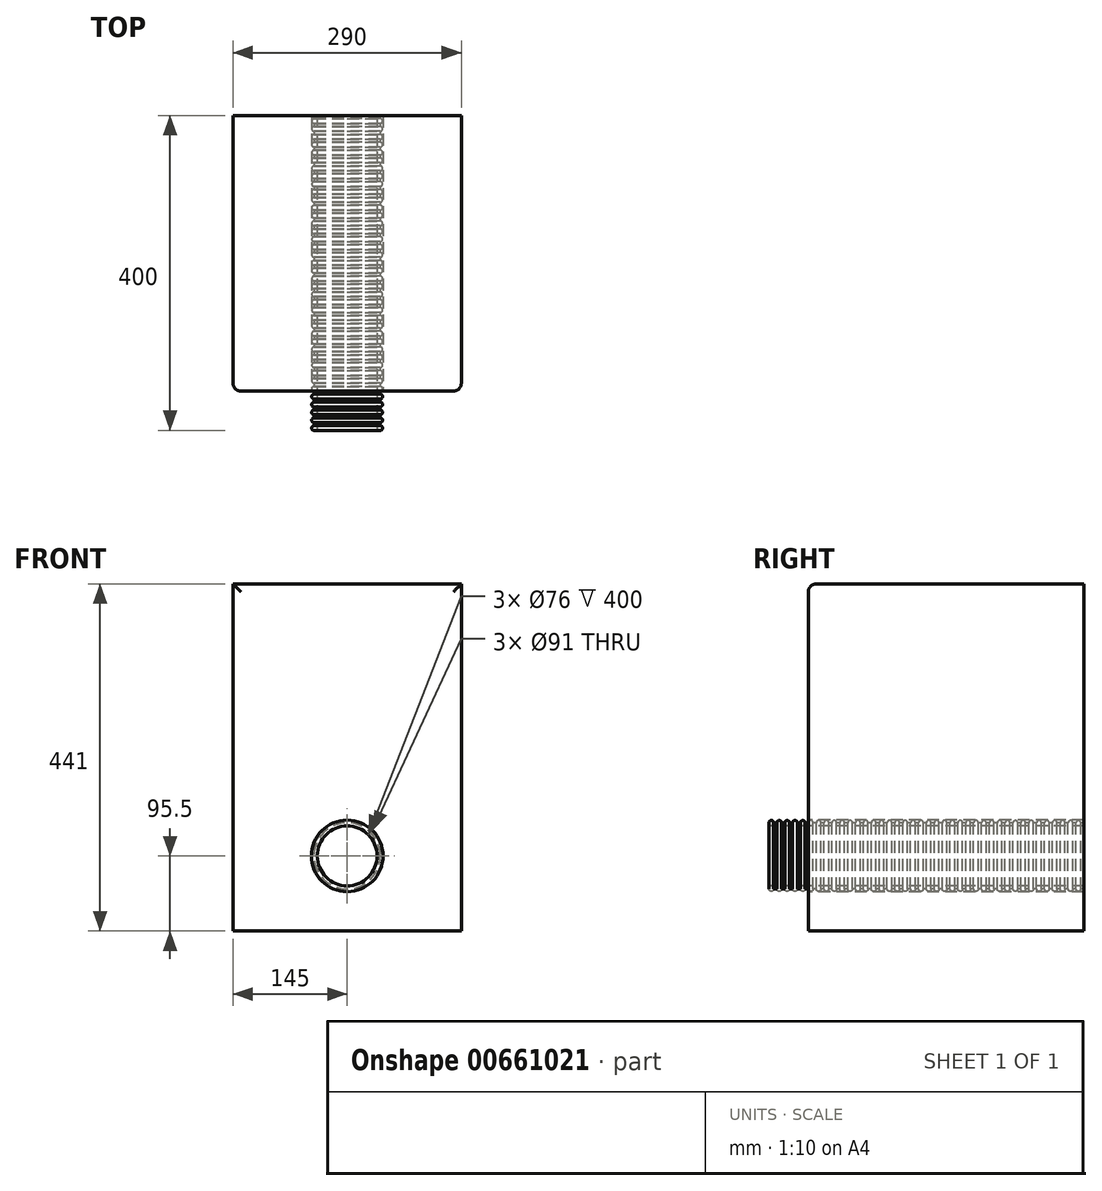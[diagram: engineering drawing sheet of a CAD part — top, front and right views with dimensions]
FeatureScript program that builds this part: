
annotation { "Feature Type Name" : "Feature", "Feature Type Description" : "" }
export const myFeature = defineFeature(function(context is Context, id is Id, definition is map)
    precondition{}
    {
        {
            var Q0;
            Q0=qCreatedBy(makeId("Right.planeOp"),FACE);
            var sketch = newSketch(context, id + "F0", { "sketchPlane" : qUnion([Q0])});
            skLineSegment(sketch, "E0", {"start": v(0, 0) * mm, "end": v(400, 0) * mm, "construction": true});
            skLineSegment(sketch, "E1", {"start": v(0, 38) * mm, "end": v(400, 38) * mm});
            skLineSegment(sketch, "E2", {"start": v(0, 38) * mm, "end": v(0, 42) * mm});
            skArc(sketch, "E3", {"start": v(6, 42) * mm, "mid": v(3, 45) * mm, "end": v(0, 42) * mm});
            skLineSegment(sketch, "E4", {"start": v(6, 42) * mm, "end": v(10, 42) * mm});
            skLineSegment(sketch, "E5.1.0.0", {"start": v(10, 38) * mm, "end": v(10, 42) * mm});
            skLineSegment(sketch, "E5.direction1", {"start": v(0, 38) * mm, "end": v(10, 38) * mm, "construction": true});
            skLineSegment(sketch, "E6.1.0.0", {"start": v(10, 38) * mm, "end": v(20, 38) * mm, "construction": true});
            skLineSegment(sketch, "E6.1.0.1", {"start": v(20, 38) * mm, "end": v(20, 42) * mm});
            skLineSegment(sketch, "E6.1.0.2", {"start": v(16, 42) * mm, "end": v(20, 42) * mm});
            skArc(sketch, "E6.1.0.3", {"start": v(16, 42) * mm, "mid": v(13, 45) * mm, "end": v(10, 42) * mm});
            skLineSegment(sketch, "E6.2.0.0", {"start": v(20, 38) * mm, "end": v(30, 38) * mm, "construction": true});
            skLineSegment(sketch, "E6.2.0.1", {"start": v(30, 38) * mm, "end": v(30, 42) * mm});
            skLineSegment(sketch, "E6.2.0.2", {"start": v(26, 42) * mm, "end": v(30, 42) * mm});
            skArc(sketch, "E6.2.0.3", {"start": v(26, 42) * mm, "mid": v(23, 45) * mm, "end": v(20, 42) * mm});
            skLineSegment(sketch, "E6.2.0.4", {"start": v(20, 38) * mm, "end": v(20, 42) * mm});
            skLineSegment(sketch, "E6.3.0.0", {"start": v(30, 38) * mm, "end": v(40, 38) * mm, "construction": true});
            skLineSegment(sketch, "E6.3.0.1", {"start": v(40, 38) * mm, "end": v(40, 42) * mm});
            skLineSegment(sketch, "E6.3.0.2", {"start": v(36, 42) * mm, "end": v(40, 42) * mm});
            skArc(sketch, "E6.3.0.3", {"start": v(36, 42) * mm, "mid": v(33, 45) * mm, "end": v(30, 42) * mm});
            skLineSegment(sketch, "E6.3.0.4", {"start": v(30, 38) * mm, "end": v(30, 42) * mm});
            skLineSegment(sketch, "E6.4.0.0", {"start": v(40, 38) * mm, "end": v(50, 38) * mm, "construction": true});
            skLineSegment(sketch, "E6.4.0.1", {"start": v(50, 38) * mm, "end": v(50, 42) * mm});
            skLineSegment(sketch, "E6.4.0.2", {"start": v(46, 42) * mm, "end": v(50, 42) * mm});
            skArc(sketch, "E6.4.0.3", {"start": v(46, 42) * mm, "mid": v(43, 45) * mm, "end": v(40, 42) * mm});
            skLineSegment(sketch, "E6.4.0.4", {"start": v(40, 38) * mm, "end": v(40, 42) * mm});
            skLineSegment(sketch, "E6.5.0.0", {"start": v(50, 38) * mm, "end": v(60, 38) * mm, "construction": true});
            skLineSegment(sketch, "E6.5.0.1", {"start": v(60, 38) * mm, "end": v(60, 42) * mm});
            skLineSegment(sketch, "E6.5.0.2", {"start": v(56, 42) * mm, "end": v(60, 42) * mm});
            skArc(sketch, "E6.5.0.3", {"start": v(56, 42) * mm, "mid": v(53, 45) * mm, "end": v(50, 42) * mm});
            skLineSegment(sketch, "E6.5.0.4", {"start": v(50, 38) * mm, "end": v(50, 42) * mm});
            skLineSegment(sketch, "E6.6.0.0", {"start": v(60, 38) * mm, "end": v(70, 38) * mm, "construction": true});
            skLineSegment(sketch, "E6.6.0.1", {"start": v(70, 38) * mm, "end": v(70, 42) * mm});
            skLineSegment(sketch, "E6.6.0.2", {"start": v(66, 42) * mm, "end": v(70, 42) * mm});
            skArc(sketch, "E6.6.0.3", {"start": v(66, 42) * mm, "mid": v(63, 45) * mm, "end": v(60, 42) * mm});
            skLineSegment(sketch, "E6.6.0.4", {"start": v(60, 38) * mm, "end": v(60, 42) * mm});
            skLineSegment(sketch, "E6.7.0.0", {"start": v(70, 38) * mm, "end": v(80, 38) * mm, "construction": true});
            skLineSegment(sketch, "E6.7.0.1", {"start": v(80, 38) * mm, "end": v(80, 42) * mm});
            skLineSegment(sketch, "E6.7.0.2", {"start": v(76, 42) * mm, "end": v(80, 42) * mm});
            skArc(sketch, "E6.7.0.3", {"start": v(76, 42) * mm, "mid": v(73, 45) * mm, "end": v(70, 42) * mm});
            skLineSegment(sketch, "E6.7.0.4", {"start": v(70, 38) * mm, "end": v(70, 42) * mm});
            skLineSegment(sketch, "E6.8.0.0", {"start": v(80, 38) * mm, "end": v(90, 38) * mm, "construction": true});
            skLineSegment(sketch, "E6.8.0.1", {"start": v(90, 38) * mm, "end": v(90, 42) * mm});
            skLineSegment(sketch, "E6.8.0.2", {"start": v(86, 42) * mm, "end": v(90, 42) * mm});
            skArc(sketch, "E6.8.0.3", {"start": v(86, 42) * mm, "mid": v(83, 45) * mm, "end": v(80, 42) * mm});
            skLineSegment(sketch, "E6.8.0.4", {"start": v(80, 38) * mm, "end": v(80, 42) * mm});
            skLineSegment(sketch, "E6.9.0.0", {"start": v(90, 38) * mm, "end": v(100, 38) * mm, "construction": true});
            skLineSegment(sketch, "E6.9.0.1", {"start": v(100, 38) * mm, "end": v(100, 42) * mm});
            skLineSegment(sketch, "E6.9.0.2", {"start": v(96, 42) * mm, "end": v(100, 42) * mm});
            skArc(sketch, "E6.9.0.3", {"start": v(96, 42) * mm, "mid": v(93, 45) * mm, "end": v(90, 42) * mm});
            skLineSegment(sketch, "E6.9.0.4", {"start": v(90, 38) * mm, "end": v(90, 42) * mm});
            skLineSegment(sketch, "E6.10.0.0", {"start": v(100, 38) * mm, "end": v(110, 38) * mm, "construction": true});
            skLineSegment(sketch, "E6.10.0.1", {"start": v(110, 38) * mm, "end": v(110, 42) * mm});
            skLineSegment(sketch, "E6.10.0.2", {"start": v(106, 42) * mm, "end": v(110, 42) * mm});
            skArc(sketch, "E6.10.0.3", {"start": v(106, 42) * mm, "mid": v(103, 45) * mm, "end": v(100, 42) * mm});
            skLineSegment(sketch, "E6.10.0.4", {"start": v(100, 38) * mm, "end": v(100, 42) * mm});
            skLineSegment(sketch, "E6.11.0.0", {"start": v(110, 38) * mm, "end": v(120, 38) * mm, "construction": true});
            skLineSegment(sketch, "E6.11.0.1", {"start": v(120, 38) * mm, "end": v(120, 42) * mm});
            skLineSegment(sketch, "E6.11.0.2", {"start": v(116, 42) * mm, "end": v(120, 42) * mm});
            skArc(sketch, "E6.11.0.3", {"start": v(116, 42) * mm, "mid": v(113, 45) * mm, "end": v(110, 42) * mm});
            skLineSegment(sketch, "E6.11.0.4", {"start": v(110, 38) * mm, "end": v(110, 42) * mm});
            skLineSegment(sketch, "E6.12.0.0", {"start": v(120, 38) * mm, "end": v(130, 38) * mm, "construction": true});
            skLineSegment(sketch, "E6.12.0.1", {"start": v(130, 38) * mm, "end": v(130, 42) * mm});
            skLineSegment(sketch, "E6.12.0.2", {"start": v(126, 42) * mm, "end": v(130, 42) * mm});
            skArc(sketch, "E6.12.0.3", {"start": v(126, 42) * mm, "mid": v(123, 45) * mm, "end": v(120, 42) * mm});
            skLineSegment(sketch, "E6.12.0.4", {"start": v(120, 38) * mm, "end": v(120, 42) * mm});
            skLineSegment(sketch, "E6.13.0.0", {"start": v(130, 38) * mm, "end": v(140, 38) * mm, "construction": true});
            skLineSegment(sketch, "E6.13.0.1", {"start": v(140, 38) * mm, "end": v(140, 42) * mm});
            skLineSegment(sketch, "E6.13.0.2", {"start": v(136, 42) * mm, "end": v(140, 42) * mm});
            skArc(sketch, "E6.13.0.3", {"start": v(136, 42) * mm, "mid": v(133, 45) * mm, "end": v(130, 42) * mm});
            skLineSegment(sketch, "E6.13.0.4", {"start": v(130, 38) * mm, "end": v(130, 42) * mm});
            skLineSegment(sketch, "E6.14.0.0", {"start": v(140, 38) * mm, "end": v(150, 38) * mm, "construction": true});
            skLineSegment(sketch, "E6.14.0.1", {"start": v(150, 38) * mm, "end": v(150, 42) * mm});
            skLineSegment(sketch, "E6.14.0.2", {"start": v(146, 42) * mm, "end": v(150, 42) * mm});
            skArc(sketch, "E6.14.0.3", {"start": v(146, 42) * mm, "mid": v(143, 45) * mm, "end": v(140, 42) * mm});
            skLineSegment(sketch, "E6.14.0.4", {"start": v(140, 38) * mm, "end": v(140, 42) * mm});
            skLineSegment(sketch, "E6.15.0.0", {"start": v(150, 38) * mm, "end": v(160, 38) * mm, "construction": true});
            skLineSegment(sketch, "E6.15.0.1", {"start": v(160, 38) * mm, "end": v(160, 42) * mm});
            skLineSegment(sketch, "E6.15.0.2", {"start": v(156, 42) * mm, "end": v(160, 42) * mm});
            skArc(sketch, "E6.15.0.3", {"start": v(156, 42) * mm, "mid": v(153, 45) * mm, "end": v(150, 42) * mm});
            skLineSegment(sketch, "E6.15.0.4", {"start": v(150, 38) * mm, "end": v(150, 42) * mm});
            skLineSegment(sketch, "E6.16.0.0", {"start": v(160, 38) * mm, "end": v(170, 38) * mm, "construction": true});
            skLineSegment(sketch, "E6.16.0.1", {"start": v(170, 38) * mm, "end": v(170, 42) * mm});
            skLineSegment(sketch, "E6.16.0.2", {"start": v(166, 42) * mm, "end": v(170, 42) * mm});
            skArc(sketch, "E6.16.0.3", {"start": v(166, 42) * mm, "mid": v(163, 45) * mm, "end": v(160, 42) * mm});
            skLineSegment(sketch, "E6.16.0.4", {"start": v(160, 38) * mm, "end": v(160, 42) * mm});
            skLineSegment(sketch, "E6.17.0.0", {"start": v(170, 38) * mm, "end": v(180, 38) * mm, "construction": true});
            skLineSegment(sketch, "E6.17.0.1", {"start": v(180, 38) * mm, "end": v(180, 42) * mm});
            skLineSegment(sketch, "E6.17.0.2", {"start": v(176, 42) * mm, "end": v(180, 42) * mm});
            skArc(sketch, "E6.17.0.3", {"start": v(176, 42) * mm, "mid": v(173, 45) * mm, "end": v(170, 42) * mm});
            skLineSegment(sketch, "E6.17.0.4", {"start": v(170, 38) * mm, "end": v(170, 42) * mm});
            skLineSegment(sketch, "E6.18.0.0", {"start": v(180, 38) * mm, "end": v(190, 38) * mm, "construction": true});
            skLineSegment(sketch, "E6.18.0.1", {"start": v(190, 38) * mm, "end": v(190, 42) * mm});
            skLineSegment(sketch, "E6.18.0.2", {"start": v(186, 42) * mm, "end": v(190, 42) * mm});
            skArc(sketch, "E6.18.0.3", {"start": v(186, 42) * mm, "mid": v(183, 45) * mm, "end": v(180, 42) * mm});
            skLineSegment(sketch, "E6.18.0.4", {"start": v(180, 38) * mm, "end": v(180, 42) * mm});
            skLineSegment(sketch, "E6.19.0.0", {"start": v(190, 38) * mm, "end": v(200, 38) * mm, "construction": true});
            skLineSegment(sketch, "E6.19.0.1", {"start": v(200, 38) * mm, "end": v(200, 42) * mm});
            skLineSegment(sketch, "E6.19.0.2", {"start": v(196, 42) * mm, "end": v(200, 42) * mm});
            skArc(sketch, "E6.19.0.3", {"start": v(196, 42) * mm, "mid": v(193, 45) * mm, "end": v(190, 42) * mm});
            skLineSegment(sketch, "E6.19.0.4", {"start": v(190, 38) * mm, "end": v(190, 42) * mm});
            skLineSegment(sketch, "E6.20.0.0", {"start": v(200, 38) * mm, "end": v(210, 38) * mm, "construction": true});
            skLineSegment(sketch, "E6.20.0.1", {"start": v(210, 38) * mm, "end": v(210, 42) * mm});
            skLineSegment(sketch, "E6.20.0.2", {"start": v(206, 42) * mm, "end": v(210, 42) * mm});
            skArc(sketch, "E6.20.0.3", {"start": v(206, 42) * mm, "mid": v(203, 45) * mm, "end": v(200, 42) * mm});
            skLineSegment(sketch, "E6.20.0.4", {"start": v(200, 38) * mm, "end": v(200, 42) * mm});
            skLineSegment(sketch, "E6.21.0.0", {"start": v(210, 38) * mm, "end": v(220, 38) * mm, "construction": true});
            skLineSegment(sketch, "E6.21.0.1", {"start": v(220, 38) * mm, "end": v(220, 42) * mm});
            skLineSegment(sketch, "E6.21.0.2", {"start": v(216, 42) * mm, "end": v(220, 42) * mm});
            skArc(sketch, "E6.21.0.3", {"start": v(216, 42) * mm, "mid": v(213, 45) * mm, "end": v(210, 42) * mm});
            skLineSegment(sketch, "E6.21.0.4", {"start": v(210, 38) * mm, "end": v(210, 42) * mm});
            skLineSegment(sketch, "E6.22.0.0", {"start": v(220, 38) * mm, "end": v(230, 38) * mm, "construction": true});
            skLineSegment(sketch, "E6.22.0.1", {"start": v(230, 38) * mm, "end": v(230, 42) * mm});
            skLineSegment(sketch, "E6.22.0.2", {"start": v(226, 42) * mm, "end": v(230, 42) * mm});
            skArc(sketch, "E6.22.0.3", {"start": v(226, 42) * mm, "mid": v(223, 45) * mm, "end": v(220, 42) * mm});
            skLineSegment(sketch, "E6.22.0.4", {"start": v(220, 38) * mm, "end": v(220, 42) * mm});
            skLineSegment(sketch, "E6.23.0.0", {"start": v(230, 38) * mm, "end": v(240, 38) * mm, "construction": true});
            skLineSegment(sketch, "E6.23.0.1", {"start": v(240, 38) * mm, "end": v(240, 42) * mm});
            skLineSegment(sketch, "E6.23.0.2", {"start": v(236, 42) * mm, "end": v(240, 42) * mm});
            skArc(sketch, "E6.23.0.3", {"start": v(236, 42) * mm, "mid": v(233, 45) * mm, "end": v(230, 42) * mm});
            skLineSegment(sketch, "E6.23.0.4", {"start": v(230, 38) * mm, "end": v(230, 42) * mm});
            skLineSegment(sketch, "E6.24.0.0", {"start": v(240, 38) * mm, "end": v(250, 38) * mm, "construction": true});
            skLineSegment(sketch, "E6.24.0.1", {"start": v(250, 38) * mm, "end": v(250, 42) * mm});
            skLineSegment(sketch, "E6.24.0.2", {"start": v(246, 42) * mm, "end": v(250, 42) * mm});
            skArc(sketch, "E6.24.0.3", {"start": v(246, 42) * mm, "mid": v(243, 45) * mm, "end": v(240, 42) * mm});
            skLineSegment(sketch, "E6.24.0.4", {"start": v(240, 38) * mm, "end": v(240, 42) * mm});
            skLineSegment(sketch, "E6.25.0.0", {"start": v(250, 38) * mm, "end": v(260, 38) * mm, "construction": true});
            skLineSegment(sketch, "E6.25.0.1", {"start": v(260, 38) * mm, "end": v(260, 42) * mm});
            skLineSegment(sketch, "E6.25.0.2", {"start": v(256, 42) * mm, "end": v(260, 42) * mm});
            skArc(sketch, "E6.25.0.3", {"start": v(256, 42) * mm, "mid": v(253, 45) * mm, "end": v(250, 42) * mm});
            skLineSegment(sketch, "E6.25.0.4", {"start": v(250, 38) * mm, "end": v(250, 42) * mm});
            skLineSegment(sketch, "E6.26.0.0", {"start": v(260, 38) * mm, "end": v(270, 38) * mm, "construction": true});
            skLineSegment(sketch, "E6.26.0.1", {"start": v(270, 38) * mm, "end": v(270, 42) * mm});
            skLineSegment(sketch, "E6.26.0.2", {"start": v(266, 42) * mm, "end": v(270, 42) * mm});
            skArc(sketch, "E6.26.0.3", {"start": v(266, 42) * mm, "mid": v(263, 45) * mm, "end": v(260, 42) * mm});
            skLineSegment(sketch, "E6.26.0.4", {"start": v(260, 38) * mm, "end": v(260, 42) * mm});
            skLineSegment(sketch, "E6.27.0.0", {"start": v(270, 38) * mm, "end": v(280, 38) * mm, "construction": true});
            skLineSegment(sketch, "E6.27.0.1", {"start": v(280, 38) * mm, "end": v(280, 42) * mm});
            skLineSegment(sketch, "E6.27.0.2", {"start": v(276, 42) * mm, "end": v(280, 42) * mm});
            skArc(sketch, "E6.27.0.3", {"start": v(276, 42) * mm, "mid": v(273, 45) * mm, "end": v(270, 42) * mm});
            skLineSegment(sketch, "E6.27.0.4", {"start": v(270, 38) * mm, "end": v(270, 42) * mm});
            skLineSegment(sketch, "E6.28.0.0", {"start": v(280, 38) * mm, "end": v(290, 38) * mm, "construction": true});
            skLineSegment(sketch, "E6.28.0.1", {"start": v(290, 38) * mm, "end": v(290, 42) * mm});
            skLineSegment(sketch, "E6.28.0.2", {"start": v(286, 42) * mm, "end": v(290, 42) * mm});
            skArc(sketch, "E6.28.0.3", {"start": v(286, 42) * mm, "mid": v(283, 45) * mm, "end": v(280, 42) * mm});
            skLineSegment(sketch, "E6.28.0.4", {"start": v(280, 38) * mm, "end": v(280, 42) * mm});
            skLineSegment(sketch, "E6.29.0.0", {"start": v(290, 38) * mm, "end": v(300, 38) * mm, "construction": true});
            skLineSegment(sketch, "E6.29.0.1", {"start": v(300, 38) * mm, "end": v(300, 42) * mm});
            skLineSegment(sketch, "E6.29.0.2", {"start": v(296, 42) * mm, "end": v(300, 42) * mm});
            skArc(sketch, "E6.29.0.3", {"start": v(296, 42) * mm, "mid": v(293, 45) * mm, "end": v(290, 42) * mm});
            skLineSegment(sketch, "E6.29.0.4", {"start": v(290, 38) * mm, "end": v(290, 42) * mm});
            skLineSegment(sketch, "E6.30.0.0", {"start": v(300, 38) * mm, "end": v(310, 38) * mm, "construction": true});
            skLineSegment(sketch, "E6.30.0.1", {"start": v(310, 38) * mm, "end": v(310, 42) * mm});
            skLineSegment(sketch, "E6.30.0.2", {"start": v(306, 42) * mm, "end": v(310, 42) * mm});
            skArc(sketch, "E6.30.0.3", {"start": v(306, 42) * mm, "mid": v(303, 45) * mm, "end": v(300, 42) * mm});
            skLineSegment(sketch, "E6.30.0.4", {"start": v(300, 38) * mm, "end": v(300, 42) * mm});
            skLineSegment(sketch, "E6.31.0.0", {"start": v(310, 38) * mm, "end": v(320, 38) * mm, "construction": true});
            skLineSegment(sketch, "E6.31.0.1", {"start": v(320, 38) * mm, "end": v(320, 42) * mm});
            skLineSegment(sketch, "E6.31.0.2", {"start": v(316, 42) * mm, "end": v(320, 42) * mm});
            skArc(sketch, "E6.31.0.3", {"start": v(316, 42) * mm, "mid": v(313, 45) * mm, "end": v(310, 42) * mm});
            skLineSegment(sketch, "E6.31.0.4", {"start": v(310, 38) * mm, "end": v(310, 42) * mm});
            skLineSegment(sketch, "E6.32.0.0", {"start": v(320, 38) * mm, "end": v(330, 38) * mm, "construction": true});
            skLineSegment(sketch, "E6.32.0.1", {"start": v(330, 38) * mm, "end": v(330, 42) * mm});
            skLineSegment(sketch, "E6.32.0.2", {"start": v(326, 42) * mm, "end": v(330, 42) * mm});
            skArc(sketch, "E6.32.0.3", {"start": v(326, 42) * mm, "mid": v(323, 45) * mm, "end": v(320, 42) * mm});
            skLineSegment(sketch, "E6.32.0.4", {"start": v(320, 38) * mm, "end": v(320, 42) * mm});
            skLineSegment(sketch, "E6.33.0.0", {"start": v(330, 38) * mm, "end": v(340, 38) * mm, "construction": true});
            skLineSegment(sketch, "E6.33.0.1", {"start": v(340, 38) * mm, "end": v(340, 42) * mm});
            skLineSegment(sketch, "E6.33.0.2", {"start": v(336, 42) * mm, "end": v(340, 42) * mm});
            skArc(sketch, "E6.33.0.3", {"start": v(336, 42) * mm, "mid": v(333, 45) * mm, "end": v(330, 42) * mm});
            skLineSegment(sketch, "E6.33.0.4", {"start": v(330, 38) * mm, "end": v(330, 42) * mm});
            skLineSegment(sketch, "E6.34.0.0", {"start": v(340, 38) * mm, "end": v(350, 38) * mm, "construction": true});
            skLineSegment(sketch, "E6.34.0.1", {"start": v(350, 38) * mm, "end": v(350, 42) * mm});
            skLineSegment(sketch, "E6.34.0.2", {"start": v(346, 42) * mm, "end": v(350, 42) * mm});
            skArc(sketch, "E6.34.0.3", {"start": v(346, 42) * mm, "mid": v(343, 45) * mm, "end": v(340, 42) * mm});
            skLineSegment(sketch, "E6.34.0.4", {"start": v(340, 38) * mm, "end": v(340, 42) * mm});
            skLineSegment(sketch, "E6.35.0.0", {"start": v(350, 38) * mm, "end": v(360, 38) * mm, "construction": true});
            skLineSegment(sketch, "E6.35.0.1", {"start": v(360, 38) * mm, "end": v(360, 42) * mm});
            skLineSegment(sketch, "E6.35.0.2", {"start": v(356, 42) * mm, "end": v(360, 42) * mm});
            skArc(sketch, "E6.35.0.3", {"start": v(356, 42) * mm, "mid": v(353, 45) * mm, "end": v(350, 42) * mm});
            skLineSegment(sketch, "E6.35.0.4", {"start": v(350, 38) * mm, "end": v(350, 42) * mm});
            skLineSegment(sketch, "E6.36.0.0", {"start": v(360, 38) * mm, "end": v(370, 38) * mm, "construction": true});
            skLineSegment(sketch, "E6.36.0.1", {"start": v(370, 38) * mm, "end": v(370, 42) * mm});
            skLineSegment(sketch, "E6.36.0.2", {"start": v(366, 42) * mm, "end": v(370, 42) * mm});
            skArc(sketch, "E6.36.0.3", {"start": v(366, 42) * mm, "mid": v(363, 45) * mm, "end": v(360, 42) * mm});
            skLineSegment(sketch, "E6.36.0.4", {"start": v(360, 38) * mm, "end": v(360, 42) * mm});
            skLineSegment(sketch, "E6.37.0.0", {"start": v(370, 38) * mm, "end": v(380, 38) * mm, "construction": true});
            skLineSegment(sketch, "E6.37.0.1", {"start": v(380, 38) * mm, "end": v(380, 42) * mm});
            skLineSegment(sketch, "E6.37.0.2", {"start": v(376, 42) * mm, "end": v(380, 42) * mm});
            skArc(sketch, "E6.37.0.3", {"start": v(376, 42) * mm, "mid": v(373, 45) * mm, "end": v(370, 42) * mm});
            skLineSegment(sketch, "E6.37.0.4", {"start": v(370, 38) * mm, "end": v(370, 42) * mm});
            skLineSegment(sketch, "E6.38.0.0", {"start": v(380, 38) * mm, "end": v(390, 38) * mm, "construction": true});
            skLineSegment(sketch, "E6.38.0.1", {"start": v(390, 38) * mm, "end": v(390, 42) * mm});
            skLineSegment(sketch, "E6.38.0.2", {"start": v(386, 42) * mm, "end": v(390, 42) * mm});
            skArc(sketch, "E6.38.0.3", {"start": v(386, 42) * mm, "mid": v(383, 45) * mm, "end": v(380, 42) * mm});
            skLineSegment(sketch, "E6.38.0.4", {"start": v(380, 38) * mm, "end": v(380, 42) * mm});
            skLineSegment(sketch, "E6.39.0.0", {"start": v(390, 38) * mm, "end": v(400, 38) * mm, "construction": true});
            skLineSegment(sketch, "E6.39.0.1", {"start": v(400, 38) * mm, "end": v(400, 42) * mm});
            skLineSegment(sketch, "E6.39.0.2", {"start": v(396, 42) * mm, "end": v(400, 42) * mm});
            skArc(sketch, "E6.39.0.3", {"start": v(396, 42) * mm, "mid": v(393, 45) * mm, "end": v(390, 42) * mm});
            skLineSegment(sketch, "E6.39.0.4", {"start": v(390, 38) * mm, "end": v(390, 42) * mm});
            skSolve(sketch);
        }
        {
            var Q0;
            {var subQ0=sQuery(id+"F0.wireOp",EDGE,"E6.39.0.1");Q0=makeQuery(id+"F0.imprint","IMPRINT",FACE,{"disambiguationData":[TD([[makeQuery(id+"F0.imprint","IMPRINT",EDGE,{"derivedFrom":subQ0}),1.0]])]});}
            var Q1;
            Q1=makeQuery(id+"F0.imprint","IMPRINT",FACE,{"disambiguationData":[TD([[makeQuery(id+"F0.imprint","IMPRINT",EDGE,{"derivedFrom":sQuery(id+"F0.wireOp",EDGE,"E6.30.0.2")}),-1.0]])]});
            var Q2;
            Q2=makeQuery(id+"F0.imprint","IMPRINT",FACE,{"disambiguationData":[TD([[makeQuery(id+"F0.imprint","IMPRINT",EDGE,{"derivedFrom":sQuery(id+"F0.wireOp",EDGE,"E6.23.0.2")}),-1.0]])]});
            var Q3;
            Q3=makeQuery(id+"F0.imprint","IMPRINT",FACE,{"disambiguationData":[TD([[makeQuery(id+"F0.imprint","IMPRINT",EDGE,{"derivedFrom":sQuery(id+"F0.wireOp",EDGE,"E6.24.0.2")}),-1.0]])]});
            var Q4;
            Q4=makeQuery(id+"F0.imprint","IMPRINT",FACE,{"disambiguationData":[TD([[makeQuery(id+"F0.imprint","IMPRINT",EDGE,{"derivedFrom":sQuery(id+"F0.wireOp",EDGE,"E6.4.0.2")}),-1.0]])]});
            var Q5;
            Q5=makeQuery(id+"F0.imprint","IMPRINT",FACE,{"disambiguationData":[TD([[makeQuery(id+"F0.imprint","IMPRINT",EDGE,{"derivedFrom":sQuery(id+"F0.wireOp",EDGE,"E6.9.0.2")}),-1.0]])]});
            var Q6;
            Q6=makeQuery(id+"F0.imprint","IMPRINT",FACE,{"disambiguationData":[TD([[makeQuery(id+"F0.imprint","IMPRINT",EDGE,{"derivedFrom":sQuery(id+"F0.wireOp",EDGE,"E6.10.0.2")}),-1.0]])]});
            var Q7;
            Q7=makeQuery(id+"F0.imprint","IMPRINT",FACE,{"disambiguationData":[TD([[makeQuery(id+"F0.imprint","IMPRINT",EDGE,{"derivedFrom":sQuery(id+"F0.wireOp",EDGE,"E6.5.0.2")}),-1.0]])]});
            var Q8;
            Q8=makeQuery(id+"F0.imprint","IMPRINT",FACE,{"disambiguationData":[TD([[makeQuery(id+"F0.imprint","IMPRINT",EDGE,{"derivedFrom":sQuery(id+"F0.wireOp",EDGE,"E6.7.0.2")}),-1.0]])]});
            var Q9;
            Q9=makeQuery(id+"F0.imprint","IMPRINT",FACE,{"disambiguationData":[TD([[makeQuery(id+"F0.imprint","IMPRINT",EDGE,{"derivedFrom":sQuery(id+"F0.wireOp",EDGE,"E6.8.0.2")}),-1.0]])]});
            var Q10;
            Q10=makeQuery(id+"F0.imprint","IMPRINT",FACE,{"disambiguationData":[TD([[makeQuery(id+"F0.imprint","IMPRINT",EDGE,{"derivedFrom":sQuery(id+"F0.wireOp",EDGE,"E6.12.0.2")}),-1.0]])]});
            var Q11;
            Q11=makeQuery(id+"F0.imprint","IMPRINT",FACE,{"disambiguationData":[TD([[makeQuery(id+"F0.imprint","IMPRINT",EDGE,{"derivedFrom":sQuery(id+"F0.wireOp",EDGE,"E6.14.0.2")}),-1.0]])]});
            var Q12;
            Q12=makeQuery(id+"F0.imprint","IMPRINT",FACE,{"disambiguationData":[TD([[makeQuery(id+"F0.imprint","IMPRINT",EDGE,{"derivedFrom":sQuery(id+"F0.wireOp",EDGE,"E6.21.0.2")}),-1.0]])]});
            var Q13;
            Q13=makeQuery(id+"F0.imprint","IMPRINT",FACE,{"disambiguationData":[TD([[makeQuery(id+"F0.imprint","IMPRINT",EDGE,{"derivedFrom":sQuery(id+"F0.wireOp",EDGE,"E6.37.0.2")}),-1.0]])]});
            var Q14;
            Q14=makeQuery(id+"F0.imprint","IMPRINT",FACE,{"disambiguationData":[TD([[makeQuery(id+"F0.imprint","IMPRINT",EDGE,{"derivedFrom":sQuery(id+"F0.wireOp",EDGE,"E6.36.0.2")}),-1.0]])]});
            var Q15;
            Q15=makeQuery(id+"F0.imprint","IMPRINT",FACE,{"disambiguationData":[TD([[makeQuery(id+"F0.imprint","IMPRINT",EDGE,{"derivedFrom":sQuery(id+"F0.wireOp",EDGE,"E6.20.0.2")}),-1.0]])]});
            var Q16;
            Q16=makeQuery(id+"F0.imprint","IMPRINT",FACE,{"disambiguationData":[TD([[makeQuery(id+"F0.imprint","IMPRINT",EDGE,{"derivedFrom":sQuery(id+"F0.wireOp",EDGE,"E6.35.0.2")}),-1.0]])]});
            var Q17;
            Q17=makeQuery(id+"F0.imprint","IMPRINT",FACE,{"disambiguationData":[TD([[makeQuery(id+"F0.imprint","IMPRINT",EDGE,{"derivedFrom":sQuery(id+"F0.wireOp",EDGE,"E6.19.0.2")}),-1.0]])]});
            var Q18;
            Q18=makeQuery(id+"F0.imprint","IMPRINT",FACE,{"disambiguationData":[TD([[makeQuery(id+"F0.imprint","IMPRINT",EDGE,{"derivedFrom":sQuery(id+"F0.wireOp",EDGE,"E6.34.0.2")}),-1.0]])]});
            var Q19;
            Q19=makeQuery(id+"F0.imprint","IMPRINT",FACE,{"disambiguationData":[TD([[makeQuery(id+"F0.imprint","IMPRINT",EDGE,{"derivedFrom":sQuery(id+"F0.wireOp",EDGE,"E6.18.0.2")}),-1.0]])]});
            var Q20;
            Q20=makeQuery(id+"F0.imprint","IMPRINT",FACE,{"disambiguationData":[TD([[makeQuery(id+"F0.imprint","IMPRINT",EDGE,{"derivedFrom":sQuery(id+"F0.wireOp",EDGE,"E6.31.0.2")}),-1.0]])]});
            var Q21;
            Q21=makeQuery(id+"F0.imprint","IMPRINT",FACE,{"disambiguationData":[TD([[makeQuery(id+"F0.imprint","IMPRINT",EDGE,{"derivedFrom":sQuery(id+"F0.wireOp",EDGE,"E6.15.0.2")}),-1.0]])]});
            var Q22;
            Q22=makeQuery(id+"F0.imprint","IMPRINT",FACE,{"disambiguationData":[TD([[makeQuery(id+"F0.imprint","IMPRINT",EDGE,{"derivedFrom":sQuery(id+"F0.wireOp",EDGE,"E6.3.0.2")}),-1.0]])]});
            var Q23;
            Q23=makeQuery(id+"F0.imprint","IMPRINT",FACE,{"disambiguationData":[TD([[makeQuery(id+"F0.imprint","IMPRINT",EDGE,{"derivedFrom":sQuery(id+"F0.wireOp",EDGE,"E6.2.0.2")}),-1.0]])]});
            var Q24;
            {var subQ0=sQuery(id+"F0.wireOp",EDGE,"E2");Q24=makeQuery(id+"F0.imprint","IMPRINT",FACE,{"disambiguationData":[TD([[makeQuery(id+"F0.imprint","IMPRINT",EDGE,{"derivedFrom":subQ0}),-1.0]])]});}
            var Q25;
            Q25=makeQuery(id+"F0.imprint","IMPRINT",FACE,{"disambiguationData":[TD([[makeQuery(id+"F0.imprint","IMPRINT",EDGE,{"derivedFrom":sQuery(id+"F0.wireOp",EDGE,"E6.26.0.2")}),-1.0]])]});
            var Q26;
            Q26=makeQuery(id+"F0.imprint","IMPRINT",FACE,{"disambiguationData":[TD([[makeQuery(id+"F0.imprint","IMPRINT",EDGE,{"derivedFrom":sQuery(id+"F0.wireOp",EDGE,"E6.28.0.2")}),-1.0]])]});
            var Q27;
            Q27=makeQuery(id+"F0.imprint","IMPRINT",FACE,{"disambiguationData":[TD([[makeQuery(id+"F0.imprint","IMPRINT",EDGE,{"derivedFrom":sQuery(id+"F0.wireOp",EDGE,"E6.25.0.2")}),-1.0]])]});
            var Q28;
            Q28=makeQuery(id+"F0.imprint","IMPRINT",FACE,{"disambiguationData":[TD([[makeQuery(id+"F0.imprint","IMPRINT",EDGE,{"derivedFrom":sQuery(id+"F0.wireOp",EDGE,"E6.6.0.2")}),-1.0]])]});
            var Q29;
            Q29=makeQuery(id+"F0.imprint","IMPRINT",FACE,{"disambiguationData":[TD([[makeQuery(id+"F0.imprint","IMPRINT",EDGE,{"derivedFrom":sQuery(id+"F0.wireOp",EDGE,"E6.38.0.2")}),-1.0]])]});
            var Q30;
            Q30=makeQuery(id+"F0.imprint","IMPRINT",FACE,{"disambiguationData":[TD([[makeQuery(id+"F0.imprint","IMPRINT",EDGE,{"derivedFrom":sQuery(id+"F0.wireOp",EDGE,"E6.22.0.2")}),-1.0]])]});
            var Q31;
            Q31=makeQuery(id+"F0.imprint","IMPRINT",FACE,{"disambiguationData":[TD([[makeQuery(id+"F0.imprint","IMPRINT",EDGE,{"derivedFrom":sQuery(id+"F0.wireOp",EDGE,"E6.11.0.2")}),-1.0]])]});
            var Q32;
            Q32=makeQuery(id+"F0.imprint","IMPRINT",FACE,{"disambiguationData":[TD([[makeQuery(id+"F0.imprint","IMPRINT",EDGE,{"derivedFrom":sQuery(id+"F0.wireOp",EDGE,"E6.33.0.2")}),-1.0]])]});
            var Q33;
            Q33=makeQuery(id+"F0.imprint","IMPRINT",FACE,{"disambiguationData":[TD([[makeQuery(id+"F0.imprint","IMPRINT",EDGE,{"derivedFrom":sQuery(id+"F0.wireOp",EDGE,"E6.17.0.2")}),-1.0]])]});
            var Q34;
            Q34=makeQuery(id+"F0.imprint","IMPRINT",FACE,{"disambiguationData":[TD([[makeQuery(id+"F0.imprint","IMPRINT",EDGE,{"derivedFrom":sQuery(id+"F0.wireOp",EDGE,"E6.32.0.2")}),-1.0]])]});
            var Q35;
            Q35=makeQuery(id+"F0.imprint","IMPRINT",FACE,{"disambiguationData":[TD([[makeQuery(id+"F0.imprint","IMPRINT",EDGE,{"derivedFrom":sQuery(id+"F0.wireOp",EDGE,"E6.16.0.2")}),-1.0]])]});
            var Q36;
            Q36=makeQuery(id+"F0.imprint","IMPRINT",FACE,{"disambiguationData":[TD([[makeQuery(id+"F0.imprint","IMPRINT",EDGE,{"derivedFrom":sQuery(id+"F0.wireOp",EDGE,"E6.1.0.2")}),-1.0]])]});
            var Q37;
            Q37=makeQuery(id+"F0.imprint","IMPRINT",FACE,{"disambiguationData":[TD([[makeQuery(id+"F0.imprint","IMPRINT",EDGE,{"derivedFrom":sQuery(id+"F0.wireOp",EDGE,"E6.27.0.2")}),-1.0]])]});
            var Q38;
            Q38=makeQuery(id+"F0.imprint","IMPRINT",FACE,{"disambiguationData":[TD([[makeQuery(id+"F0.imprint","IMPRINT",EDGE,{"derivedFrom":sQuery(id+"F0.wireOp",EDGE,"E6.13.0.2")}),-1.0]])]});
            var Q39;
            Q39=makeQuery(id+"F0.imprint","IMPRINT",FACE,{"disambiguationData":[TD([[makeQuery(id+"F0.imprint","IMPRINT",EDGE,{"derivedFrom":sQuery(id+"F0.wireOp",EDGE,"E6.29.0.2")}),-1.0]])]});
            var Q40;
            Q40=sQuery(id+"F0.wireOp",EDGE,"E0");
            revolve(context, id + "F1", {"surfaceOperationType" : NewSurfaceOperationType.NEW, "entities" : qUnion([Q0, Q1, Q2, Q3, Q4, Q5, Q6, Q7, Q8, Q9, Q10, Q11, Q12, Q13, Q14, Q15, Q16, Q17, Q18, Q19, Q20, Q21, Q22, Q23, Q24, Q25, Q26, Q27, Q28, Q29, Q30, Q31, Q32, Q33, Q34, Q35, Q36, Q37, Q38, Q39]), "axis" : qUnion([Q40]), "revolveType" : RevolveType.FULL});
        }
        {
            var Q0;
            Q0=qCreatedBy(makeId("Front.planeOp"),FACE);
            var sketch = newSketch(context, id + "F2", { "sketchPlane" : qUnion([Q0])});
            skCircle(sketch, "E7", {"center": v(0, 0) * mm, "radius": 45.5 * mm});
            skLineSegment(sketch, "E8.bottom", {"start": v(145, -95.5) * mm, "end": v(-145, -95.5) * mm});
            skLineSegment(sketch, "E9", {"start": v(-145, -95.5) * mm, "end": v(-145, 345.5) * mm});
            skLineSegment(sketch, "E10", {"start": v(-145, 345.5) * mm, "end": v(145, 345.5) * mm});
            skLineSegment(sketch, "E11", {"start": v(145, 345.5) * mm, "end": v(145, -95.5) * mm});
            skSolve(sketch);
        }
        {
            var Q0;
            Q0 = qSketchRegion(id + "F2", true);
            extrude(context, id + "F3", {"entities" : qUnion([Q0]), "oppositeDirection" : true, "depth" : 400 * mm, "offsetDistance" : 25 * mm, "hasSecondDirection" : true, "secondDirectionOppositeDirection" : true, "secondDirectionDepth" : 50 * mm});
        }
        {
            var Q0;
            Q0=makeQuery(id+"F3.opExtrude","CAP_EDGE",EDGE,{"disambiguationData":[OSD([sQuery(id+"F2.wireOp",EDGE,"E10")])],"isStart":true});
            var Q1;
            Q1=makeQuery(id+"F3.opExtrude","CAP_EDGE",EDGE,{"disambiguationData":[OSD([sQuery(id+"F2.wireOp",EDGE,"E11")])],"isStart":true});
            var Q2;
            Q2=makeQuery(id+"F3.opExtrude","CAP_EDGE",EDGE,{"disambiguationData":[OSD([sQuery(id+"F2.wireOp",EDGE,"E9")])],"isStart":true});
            fillet(context, id + "F4", {"entities" : qUnion([Q0, Q1, Q2]), "radius" : 10 * mm, "tangentPropagation" : true, "allowEdgeOverflow" : false});
        }
    });
